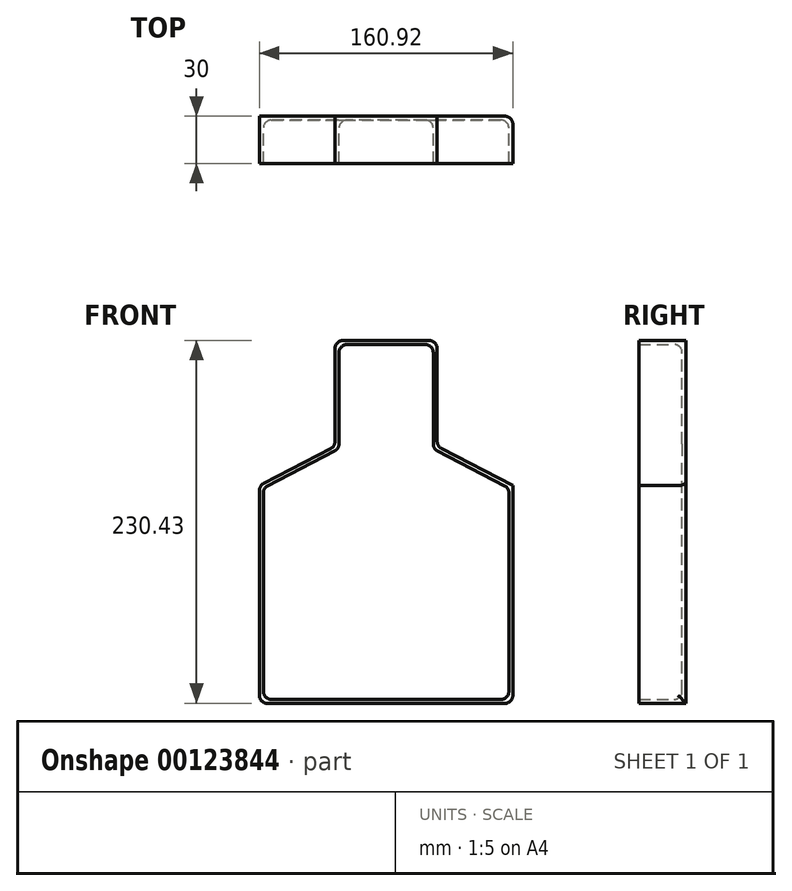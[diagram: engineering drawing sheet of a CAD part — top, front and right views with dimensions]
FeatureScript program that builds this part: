
annotation { "Feature Type Name" : "Feature", "Feature Type Description" : "" }
export const myFeature = defineFeature(function(context is Context, id is Id, definition is map)
    precondition{}
    {
        {
            var Q0;
            Q0=qCreatedBy(makeId("Front.planeOp"),FACE);
            var sketch = newSketch(context, id + "F0", { "sketchPlane" : qUnion([Q0])});
            skLineSegment(sketch, "E0", {"start": v(-80.46, -90.24) * mm, "end": v(80.46, -90.24) * mm});
            skLineSegment(sketch, "E1", {"start": v(80.46, -90.24) * mm, "end": v(80.46, 48.04) * mm});
            skLineSegment(sketch, "E2", {"start": v(80.46, 48.04) * mm, "end": v(32.44, 72.99) * mm});
            skLineSegment(sketch, "E3", {"start": v(32.44, 72.99) * mm, "end": v(32.44, 140.19) * mm});
            skLineSegment(sketch, "E4", {"start": v(32.44, 140.19) * mm, "end": v(-32.44, 140.19) * mm});
            skLineSegment(sketch, "E5", {"start": v(-32.44, 140.19) * mm, "end": v(-32.44, 72.99) * mm});
            skLineSegment(sketch, "E6", {"start": v(-32.44, 72.99) * mm, "end": v(-80.46, 48.04) * mm});
            skLineSegment(sketch, "E7", {"start": v(-80.46, 48.04) * mm, "end": v(-80.46, -90.24) * mm});
            skLineSegment(sketch, "E8", {"start": v(0, 140.19) * mm, "end": v(0, -90.24) * mm, "construction": true});
            skLineSegment(sketch, "E9", {"start": v(-80.46, 0) * mm, "end": v(80.46, 0) * mm, "construction": true});
            skSolve(sketch);
        }
        {
            var Q0;
            Q0 = qSketchRegion(id + "F0", true);
            extrude(context, id + "F1", {"entities" : qUnion([Q0]), "depth" : 30 * mm});
        }
        {
            var Q0;
            Q0=makeQuery(id+"F1.opExtrude","CAP_FACE",FACE,{"disambiguationData":[OSD([sQuery(id+"F0.wireOp",EDGE,"E0"),sQuery(id+"F0.wireOp",EDGE,"E1"),sQuery(id+"F0.wireOp",EDGE,"E2"),sQuery(id+"F0.wireOp",EDGE,"E3"),sQuery(id+"F0.wireOp",EDGE,"E4"),sQuery(id+"F0.wireOp",EDGE,"E5"),sQuery(id+"F0.wireOp",EDGE,"E6"),sQuery(id+"F0.wireOp",EDGE,"E7")])],"isStart":false});
            shell(context, id + "F2", {"entities" : qUnion([Q0]), "thickness" : 2.5 * mm});
        }
        {
            var Q0;
            {var subQ0=sQuery(id+"F0.wireOp",EDGE,"E7");Q0=makeQuery(id+"F2.opShell","OFFSET_EDGE",EDGE,{"disambiguationData":[OSD([subQ0]),TDD([makeQuery(id+"F1.opExtrude","CAP_EDGE",EDGE,{"disambiguationData":[OSD([subQ0])],"isStart":true})])]});}
            var Q1;
            {var subQ0=sQuery(id+"F0.wireOp",EDGE,"E6");Q1=makeQuery(id+"F2.opShell","OFFSET_EDGE",EDGE,{"disambiguationData":[OSD([subQ0]),TDD([makeQuery(id+"F1.opExtrude","CAP_EDGE",EDGE,{"disambiguationData":[OSD([subQ0])],"isStart":true})])]});}
            var Q2;
            {var subQ0=sQuery(id+"F0.wireOp",EDGE,"E5");Q2=makeQuery(id+"F2.opShell","OFFSET_EDGE",EDGE,{"disambiguationData":[OSD([subQ0]),TDD([makeQuery(id+"F1.opExtrude","CAP_EDGE",EDGE,{"disambiguationData":[OSD([subQ0])],"isStart":true})])]});}
            var Q3;
            {var subQ0=sQuery(id+"F0.wireOp",EDGE,"E4");Q3=makeQuery(id+"F2.opShell","OFFSET_EDGE",EDGE,{"disambiguationData":[OSD([subQ0]),TDD([makeQuery(id+"F1.opExtrude","CAP_EDGE",EDGE,{"disambiguationData":[OSD([subQ0])],"isStart":true})])]});}
            var Q4;
            Q4=makeQuery(id+"F2.opShell","OFFSET_EDGE",EDGE,{"disambiguationData":[OSD([sQuery(id+"F0.wireOp",EDGE,"E3"),sQuery(id+"F0.wireOp",EDGE,"E4")])]});
            var Q5;
            {var subQ0=sQuery(id+"F0.wireOp",EDGE,"E3");Q5=makeQuery(id+"F2.opShell","OFFSET_EDGE",EDGE,{"disambiguationData":[OSD([subQ0]),TDD([makeQuery(id+"F1.opExtrude","CAP_EDGE",EDGE,{"disambiguationData":[OSD([subQ0])],"isStart":true})])]});}
            var Q6;
            {var subQ0=sQuery(id+"F0.wireOp",EDGE,"E2");Q6=makeQuery(id+"F2.opShell","OFFSET_EDGE",EDGE,{"disambiguationData":[OSD([subQ0]),TDD([makeQuery(id+"F1.opExtrude","CAP_EDGE",EDGE,{"disambiguationData":[OSD([subQ0])],"isStart":true})])]});}
            var Q7;
            Q7=makeQuery(id+"F2.opShell","OFFSET_EDGE",EDGE,{"disambiguationData":[OSD([sQuery(id+"F0.wireOp",EDGE,"E2"),sQuery(id+"F0.wireOp",EDGE,"E3")])]});
            var Q8;
            Q8=makeQuery(id+"F2.opShell","OFFSET_EDGE",EDGE,{"disambiguationData":[OSD([sQuery(id+"F0.wireOp",EDGE,"E5"),sQuery(id+"F0.wireOp",EDGE,"E6")])]});
            var Q9;
            Q9=makeQuery(id+"F2.opShell","OFFSET_EDGE",EDGE,{"disambiguationData":[OSD([sQuery(id+"F0.wireOp",EDGE,"E0"),sQuery(id+"F0.wireOp",EDGE,"E7")])]});
            var Q10;
            {var subQ0=sQuery(id+"F0.wireOp",EDGE,"E0");Q10=makeQuery(id+"F2.opShell","OFFSET_EDGE",EDGE,{"disambiguationData":[OSD([subQ0]),TDD([makeQuery(id+"F1.opExtrude","CAP_EDGE",EDGE,{"disambiguationData":[OSD([subQ0])],"isStart":true})])]});}
            var Q11;
            Q11=makeQuery(id+"F2.opShell","OFFSET_EDGE",EDGE,{"disambiguationData":[OSD([sQuery(id+"F0.wireOp",EDGE,"E0"),sQuery(id+"F0.wireOp",EDGE,"E1")])]});
            var Q12;
            {var subQ0=sQuery(id+"F0.wireOp",EDGE,"E1");Q12=makeQuery(id+"F2.opShell","OFFSET_EDGE",EDGE,{"disambiguationData":[OSD([subQ0]),TDD([makeQuery(id+"F1.opExtrude","CAP_EDGE",EDGE,{"disambiguationData":[OSD([subQ0])],"isStart":true})])]});}
            var Q13;
            Q13=makeQuery(id+"F2.opShell","OFFSET_EDGE",EDGE,{"disambiguationData":[OSD([sQuery(id+"F0.wireOp",EDGE,"E6"),sQuery(id+"F0.wireOp",EDGE,"E7")])]});
            var Q14;
            Q14=makeQuery(id+"F2.opShell","OFFSET_EDGE",EDGE,{"disambiguationData":[OSD([sQuery(id+"F0.wireOp",EDGE,"E4"),sQuery(id+"F0.wireOp",EDGE,"E5")])]});
            var Q15;
            Q15=makeQuery(id+"F2.opShell","OFFSET_EDGE",EDGE,{"disambiguationData":[OSD([sQuery(id+"F0.wireOp",EDGE,"E1"),sQuery(id+"F0.wireOp",EDGE,"E2")])]});
            fillet(context, id + "F3", {"entities" : qUnion([Q0, Q1, Q2, Q3, Q4, Q5, Q6, Q7, Q8, Q9, Q10, Q11, Q12, Q13, Q14, Q15]), "radius" : 5 * mm, "tangentPropagation" : true, "allowEdgeOverflow" : false});
        }
        {
            var Q0;
            Q0=makeQuery(id+"F1.opExtrude","SWEPT_EDGE",EDGE,{"disambiguationData":[OSD([sQuery(id+"F0.wireOp",EDGE,"E3"),sQuery(id+"F0.wireOp",EDGE,"E4")])]});
            var Q1;
            Q1=makeQuery(id+"F1.opExtrude","CAP_EDGE",EDGE,{"disambiguationData":[OSD([sQuery(id+"F0.wireOp",EDGE,"E1")])],"isStart":true});
            var Q2;
            Q2=makeQuery(id+"F1.opExtrude","SWEPT_EDGE",EDGE,{"disambiguationData":[OSD([sQuery(id+"F0.wireOp",EDGE,"E4"),sQuery(id+"F0.wireOp",EDGE,"E5")])]});
            var Q3;
            Q3=makeQuery(id+"F1.opExtrude","SWEPT_EDGE",EDGE,{"disambiguationData":[OSD([sQuery(id+"F0.wireOp",EDGE,"E5"),sQuery(id+"F0.wireOp",EDGE,"E6")])]});
            var Q4;
            Q4=makeQuery(id+"F1.opExtrude","SWEPT_EDGE",EDGE,{"disambiguationData":[OSD([sQuery(id+"F0.wireOp",EDGE,"E2"),sQuery(id+"F0.wireOp",EDGE,"E3")])]});
            var Q5;
            Q5=makeQuery(id+"F1.opExtrude","SWEPT_EDGE",EDGE,{"disambiguationData":[OSD([sQuery(id+"F0.wireOp",EDGE,"E6"),sQuery(id+"F0.wireOp",EDGE,"E7")])]});
            var Q6;
            Q6=makeQuery(id+"F1.opExtrude","SWEPT_EDGE",EDGE,{"disambiguationData":[OSD([sQuery(id+"F0.wireOp",EDGE,"E0"),sQuery(id+"F0.wireOp",EDGE,"E7")])]});
            var Q7;
            Q7=makeQuery(id+"F1.opExtrude","SWEPT_EDGE",EDGE,{"disambiguationData":[OSD([sQuery(id+"F0.wireOp",EDGE,"E0"),sQuery(id+"F0.wireOp",EDGE,"E1")])]});
            fillet(context, id + "F4", {"entities" : qUnion([Q0, Q1, Q2, Q3, Q4, Q5, Q6, Q7]), "radius" : 5 * mm, "tangentPropagation" : true, "allowEdgeOverflow" : false});
        }
    });
